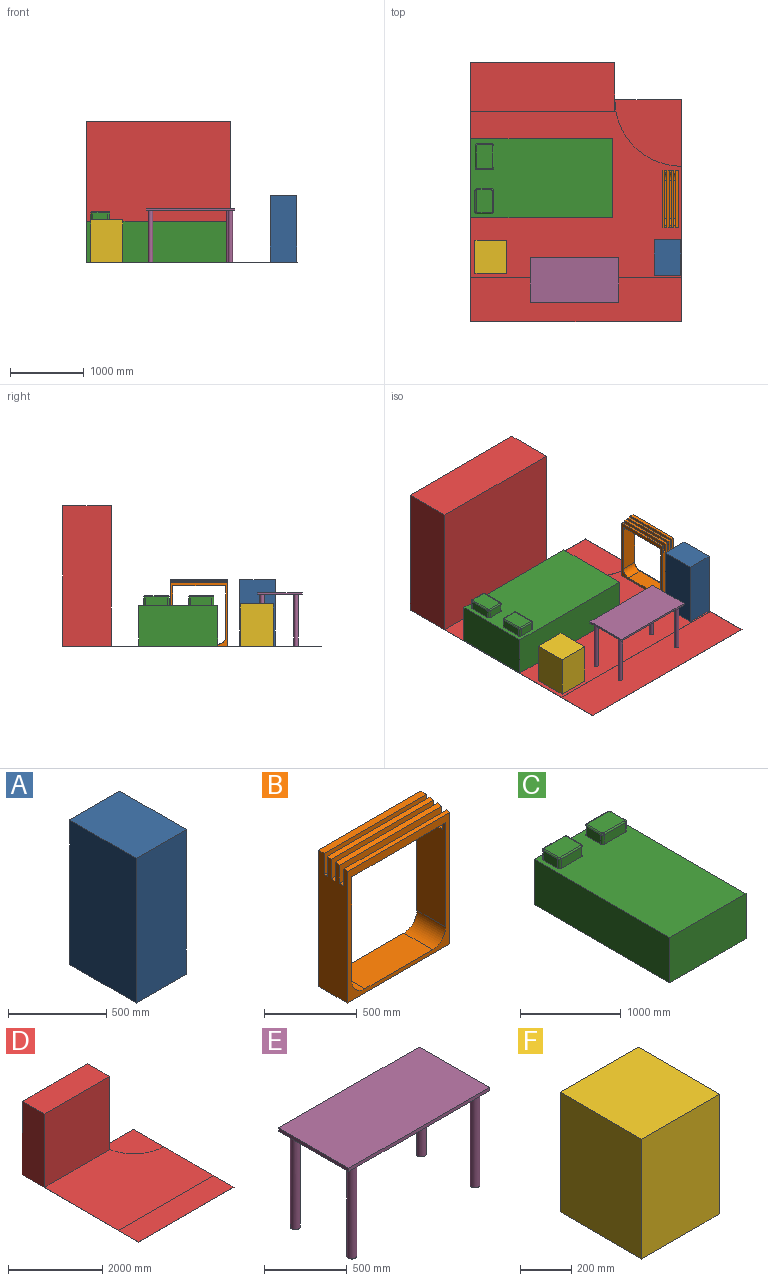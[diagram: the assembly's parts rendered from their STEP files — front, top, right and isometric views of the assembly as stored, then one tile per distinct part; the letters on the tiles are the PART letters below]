
ASSEMBLY  parts=6 mates=5
PART A: 6 faces, bbox 360x480x900 mm
  f0: plane 900x480mm, normal (1,0,0), area 432000mm2, adj f1,f3,f4,f5
  f1: plane 900x360mm, normal (0,1,0), area 324000mm2, adj f0,f2,f4,f5
  f2: plane 900x480mm, normal (-1,0,0), area 432000mm2, adj f1,f3,f4,f5
  f3: plane 900x360mm, normal (0,-1,0), area 324000mm2, adj f0,f2,f4,f5
  f4: plane 480x360mm, normal (0,0,1), area 172800mm2, adj f0,f1,f2,f3
  f5: plane 480x360mm, normal (0,0,-1), area 172800mm2, adj f0,f1,f2,f3
PART B: 30 faces, bbox 780x220x900 mm
  f0: plane 900x220mm, normal (-1,0,0), area 183895.3mm2, adj f6,f7,f8,f10,f11,f12,f15,f17
  f1: plane 715.66x44.18mm, normal (0,0,-1), area 31617.5mm2, adj f4,f5,f10,f24
  f2: plane 715.66x32.1mm, normal (0,0,-1), area 22972.6mm2, adj f4,f5,f17,f22
  f3: plane 715.66x25.35mm, normal (0,0,-1), area 18139.2mm2, adj f4,f5,f11,f21
  f4: plane 688.26x220mm, normal (-1,0,0), area 146486.9mm2, adj f1,f2,f3,f10,f11,f13,f16,f17
  f5: plane 688.26x220mm, normal (1,0,0), area 146486.9mm2, adj f1,f2,f3,f10,f11,f13,f17,f18
  f6: plane 780x32.1mm, normal (0,-0.18,0.98), area 25465.9mm2, adj f0,f9,f17,f22
  f7: plane 780x25.35mm, normal (0,-0.18,0.98), area 20107.9mm2, adj f0,f9,f11,f21
  f8: plane 780x44.18mm, normal (0,0,1), area 34459.9mm2, adj f0,f9,f10,f24
  f9: plane 900x220mm, normal (1,0,0), area 183895.3mm2, adj f6,f7,f8,f10,f11,f12,f15,f16
  f10: plane 900x780mm, normal (0,1,0), area 142161.9mm2, adj f0,f1,f4,f5,f8,f9,f12,f14
  f11: plane 867.35x780mm, normal (0,-1,0), area 116696.5mm2, adj f0,f3,f4,f5,f7,f9,f12,f14
  f12: plane 780x220mm, normal (0,0,-1), area 171600mm2, adj f0,f9,f10,f11
  f13: plane 715.66x28.9mm, normal (0,0,-1), area 20684.3mm2, adj f4,f5,f18,f26
  f14: plane 515.66x220mm, normal (0,0,1), area 113445.4mm2, adj f10,f11,f28,f29
  f15: plane 780x28.9mm, normal (0,-0.18,0.98), area 22929.2mm2, adj f0,f9,f18,f26
  f16: plane 29.64x27.49mm, normal (0,0,1), area 814.8mm2, adj f4,f9,f17,f18
  f17: plane 780x124.59mm, normal (0,1,0), area 57735.4mm2, adj f0,f2,f4,f5,f6,f9,f16,f19
  f18: plane 780x129.69mm, normal (0,-1,0), area 61716.8mm2, adj f0,f4,f5,f9,f13,f15,f16,f19
  f19: plane 34.7x27.49mm, normal (0,0,1), area 953.8mm2, adj f0,f5,f17,f18
  f20: plane 35.38x29.64mm, normal (0,0,1), area 1048.6mm2, adj f4,f9,f21,f22
  f21: plane 780x112.06mm, normal (0,1,0), area 47962mm2, adj f0,f3,f4,f5,f7,f9,f20,f23
  f22: plane 780x118.63mm, normal (0,-1,0), area 53086.2mm2, adj f0,f2,f4,f5,f6,f9,f20,f23
  f23: plane 35.38x34.7mm, normal (0,0,1), area 1227.6mm2, adj f0,f5,f21,f22
  f24: plane 780x140mm, normal (0,-1,0), area 69756.3mm2, adj f0,f1,f4,f5,f8,f9,f25,f27
  f25: plane 29.64x26.61mm, normal (0,0,1), area 788.6mm2, adj f4,f9,f24,f26
  f26: plane 780x135.06mm, normal (0,1,0), area 65902.9mm2, adj f0,f4,f5,f9,f13,f15,f25,f27
  f27: plane 34.7x26.61mm, normal (0,0,1), area 923.2mm2, adj f0,f5,f24,f26
  f28: cylinder r=100mm len=220mm, axis (0,-1,0), area 34557.5mm2, adj f4,f10,f11,f14
  f29: cylinder r=100mm len=220mm, axis (0,1,0), area 34557.5mm2, adj f5,f10,f11,f14
PART C: 40 faces, bbox 1070x1910x680 mm
  f0: plane 316.25x223.03mm, normal (0,0,1), area 70447.6mm2, adj f20,f21,f22,f23,f33,f35,f37,f39
  f1: plane 307.37x218.59mm, normal (0,0,1), area 67103mm2, adj f16,f17,f18,f19,f25,f27,f29,f31
  f2: plane 1910x1070mm, normal (0,0,1), area 1873293.4mm2, adj f3,f4,f5,f6,f8,f9,f10,f11
  f3: plane 1910x550mm, normal (1,0,0), area 1050500mm2, adj f2,f4,f6,f7
  f4: plane 1070x550mm, normal (0,1,0), area 588500mm2, adj f2,f3,f5,f7
  f5: plane 1910x550mm, normal (-1,0,0), area 1050500mm2, adj f2,f4,f6,f7
  f6: plane 1070x550mm, normal (0,-1,0), area 588500mm2, adj f2,f3,f5,f7
  f7: plane 1910x1070mm, normal (0,0,-1), area 2043700mm2, adj f3,f4,f5,f6
  f8: plane 198.59x115mm, normal (-1,0,0), area 22837.9mm2, adj f2,f17,f26,f30
  f9: plane 287.37x115mm, normal (0,-1,0), area 33047.9mm2, adj f2,f19,f24,f26
  f10: plane 198.59x115mm, normal (1,0,0), area 22837.9mm2, adj f2,f18,f24,f28
  f11: plane 287.37x115mm, normal (0,1,0), area 33047.9mm2, adj f2,f16,f28,f30
  f12: plane 203.03x115mm, normal (-1,0,0), area 23348.4mm2, adj f2,f20,f36,f38
  f13: plane 296.25x115mm, normal (0,-1,0), area 34068.9mm2, adj f2,f22,f34,f36
  f14: plane 203.03x115mm, normal (1,0,0), area 23348.4mm2, adj f2,f23,f32,f34
  f15: plane 296.25x115mm, normal (0,1,0), area 34068.9mm2, adj f2,f21,f32,f38
  f16: cylinder r=15mm len=287.37mm, axis (1,0,0), area 6771.1mm2, adj f1,f11,f29,f31
  f17: cylinder r=15mm len=198.59mm, axis (0,1,0), area 4679.2mm2, adj f1,f8,f27,f31
  f18: cylinder r=15mm len=198.59mm, axis (0,-1,0), area 4679.2mm2, adj f1,f10,f25,f29
  f19: cylinder r=15mm len=287.37mm, axis (-1,0,0), area 6771.1mm2, adj f1,f9,f25,f27
  f20: cylinder r=15mm len=203.03mm, axis (0,1,0), area 4783.8mm2, adj f0,f12,f37,f39
  f21: cylinder r=15mm len=296.25mm, axis (1,0,0), area 6980.3mm2, adj f0,f15,f33,f39
  f22: cylinder r=15mm len=296.25mm, axis (-1,0,0), area 6980.3mm2, adj f0,f13,f35,f37
  f23: cylinder r=15mm len=203.03mm, axis (0,-1,0), area 4783.8mm2, adj f0,f14,f33,f35
  f24: cylinder r=25mm len=115mm, axis (0,0,1), area 4516mm2, adj f2,f9,f10,f25
  f25: torus R=10mm, axis (0,0,1), area 723.5mm2, adj f1,f18,f19,f24
  f26: cylinder r=25mm len=115mm, axis (0,0,-1), area 4516mm2, adj f2,f8,f9,f27
  f27: torus R=10mm, axis (0,0,1), area 723.5mm2, adj f1,f17,f19,f26
  f28: cylinder r=25mm len=115mm, axis (0,0,-1), area 4516mm2, adj f2,f10,f11,f29
  f29: torus R=10mm, axis (0,0,1), area 723.5mm2, adj f1,f16,f18,f28
  f30: cylinder r=25mm len=115mm, axis (0,0,1), area 4516mm2, adj f2,f8,f11,f31
  f31: torus R=10mm, axis (0,0,1), area 723.5mm2, adj f1,f16,f17,f30
  f32: cylinder r=25mm len=115mm, axis (0,0,-1), area 4516mm2, adj f2,f14,f15,f33
  f33: torus R=10mm, axis (0,0,1), area 723.5mm2, adj f0,f21,f23,f32
  f34: cylinder r=25mm len=115mm, axis (0,0,1), area 4516mm2, adj f2,f13,f14,f35
  f35: torus R=10mm, axis (0,0,1), area 723.5mm2, adj f0,f22,f23,f34
  f36: cylinder r=25mm len=115mm, axis (0,0,-1), area 4516mm2, adj f2,f12,f13,f37
  f37: torus R=10mm, axis (0,0,1), area 723.5mm2, adj f0,f20,f22,f36
  f38: cylinder r=25mm len=115mm, axis (0,0,1), area 4516mm2, adj f2,f12,f15,f39
  f39: torus R=10mm, axis (0,0,1), area 723.5mm2, adj f0,f20,f21,f38
PART D: 14 faces, bbox 2850x3500x1903 mm
  f0: plane 3000x3mm, normal (1,0,0), area 7500mm2, adj f1,f2,f3,f7,f10,f11,f12,f13
  f1: plane 2850x2mm, normal (0,-1,0), area 5700mm2, adj f0,f3,f5,f13
  f2: plane 2850x2400mm, normal (0,0,1), area 5891827.5mm2, adj f0,f5,f6,f8,f10,f12
  f3: plane 3500x2850mm, normal (0,0,-1), area 9525000mm2, adj f0,f1,f4,f5,f6,f7
  f4: plane 1950x1903mm, normal (0,1,0), area 3710850mm2, adj f3,f5,f6,f9
  f5: plane 3500x1903mm, normal (-1,0,0), area 1263900mm2, adj f1,f2,f3,f4,f8,f9,f12,f13
  f6: plane 1903x660mm, normal (1,0,0), area 1255500mm2, adj f2,f3,f4,f7,f8,f9,f10
  f7: plane 900x2mm, normal (0,1,0), area 1800mm2, adj f0,f3,f6,f11
  f8: plane 1950x1900mm, normal (0,-1,0), area 3705000mm2, adj f2,f5,f6,f9
  f9: plane 1950x660mm, normal (0,0,1), area 1287000mm2, adj f4,f5,f6,f8
  f10: cylinder r=900mm len=900mm, axis (0,0,1), area 1413.7mm2, adj f0,f2,f6,f11
  f11: plane 900x900mm, normal (0,0,1), area 636172.5mm2, adj f0,f7,f10
  f12: plane 2850x1mm, normal (0,-1,0), area 2850mm2, adj f0,f2,f5,f13
  f13: plane 2850x600mm, normal (0,0,1), area 1710000mm2, adj f0,f1,f5,f12
PART E: 14 faces, bbox 1200x600x725 mm
  f0: plane 1200x25mm, normal (0,-1,0), area 30000mm2, adj f1,f3,f4,f5
  f1: plane 600x25mm, normal (1,0,0), area 15000mm2, adj f0,f2,f4,f5
  f2: plane 1200x25mm, normal (0,1,0), area 30000mm2, adj f1,f3,f4,f5
  f3: plane 600x25mm, normal (-1,0,0), area 15000mm2, adj f0,f2,f4,f5
  f4: plane 1200x600mm, normal (0,0,1), area 720000mm2, adj f0,f1,f2,f3
  f5: plane 1200x600mm, normal (0,0,-1), area 708690.3mm2, adj f0,f1,f2,f3,f6,f8,f10,f12
  f6: cylinder r=30mm len=700mm, axis (0,0,1), area 131946.9mm2, adj f5,f7
  f7: plane 60x60mm, normal (0,0,-1), area 2827.4mm2, adj f6
  f8: cylinder r=30mm len=700mm, axis (0,0,1), area 131946.9mm2, adj f5,f9
  f9: plane 60x60mm, normal (0,0,-1), area 2827.4mm2, adj f8
  f10: cylinder r=30mm len=700mm, axis (0,0,1), area 131946.9mm2, adj f5,f11
  f11: plane 60x60mm, normal (0,0,-1), area 2827.4mm2, adj f10
  f12: cylinder r=30mm len=700mm, axis (0,0,1), area 131946.9mm2, adj f5,f13
  f13: plane 60x60mm, normal (0,0,-1), area 2827.4mm2, adj f12
PART F: 6 faces, bbox 430x450x570 mm
  f0: plane 570x450mm, normal (1,0,0), area 256500mm2, adj f1,f3,f4,f5
  f1: plane 570x430mm, normal (0,1,0), area 245100mm2, adj f0,f2,f4,f5
  f2: plane 570x450mm, normal (-1,0,0), area 256500mm2, adj f1,f3,f4,f5
  f3: plane 570x430mm, normal (0,-1,0), area 245100mm2, adj f0,f2,f4,f5
  f4: plane 450x430mm, normal (0,0,1), area 193500mm2, adj f0,f1,f2,f3
  f5: plane 450x430mm, normal (0,0,-1), area 193500mm2, adj f0,f1,f2,f3
PLACE A t=(1206.77,-1280.98,-996.15)mm
PLACE B rot(axis=(0,0,-1),90deg) t=(955.05,-637.42,-996.15)mm
PLACE C rot(axis=(0,0,1),90deg) t=(276.61,567.28,-996.15)mm
PLACE D t=(-1637.51,1595.54,-999.15)mm fixed
PLACE E rot(axis=(0,0,-1),180deg) t=(-234.63,-1343.88,-296.15)mm
PLACE F t=(-1148.88,-1254.1,-996.15)mm
MATE planar E.f6 <-> D.f2  axis (0,0,-1) through (-774.63,-1103.88,-996.15)mm
MATE planar B.f12 <-> D.f2  axis (0,0,-1) through (1065.05,-247.42,-996.15)mm
MATE planar C.f7 <-> D.f2  axis (0,0,-1) through (-678.39,32.28,-996.15)mm
MATE planar F.f5 <-> D.f2  axis (0,0,-1) through (-1363.88,-1029.1,-996.15)mm
MATE planar D.f2 <-> A.f5  axis (0,0,1) through (-301.3,-252.09,-996.15)mm
